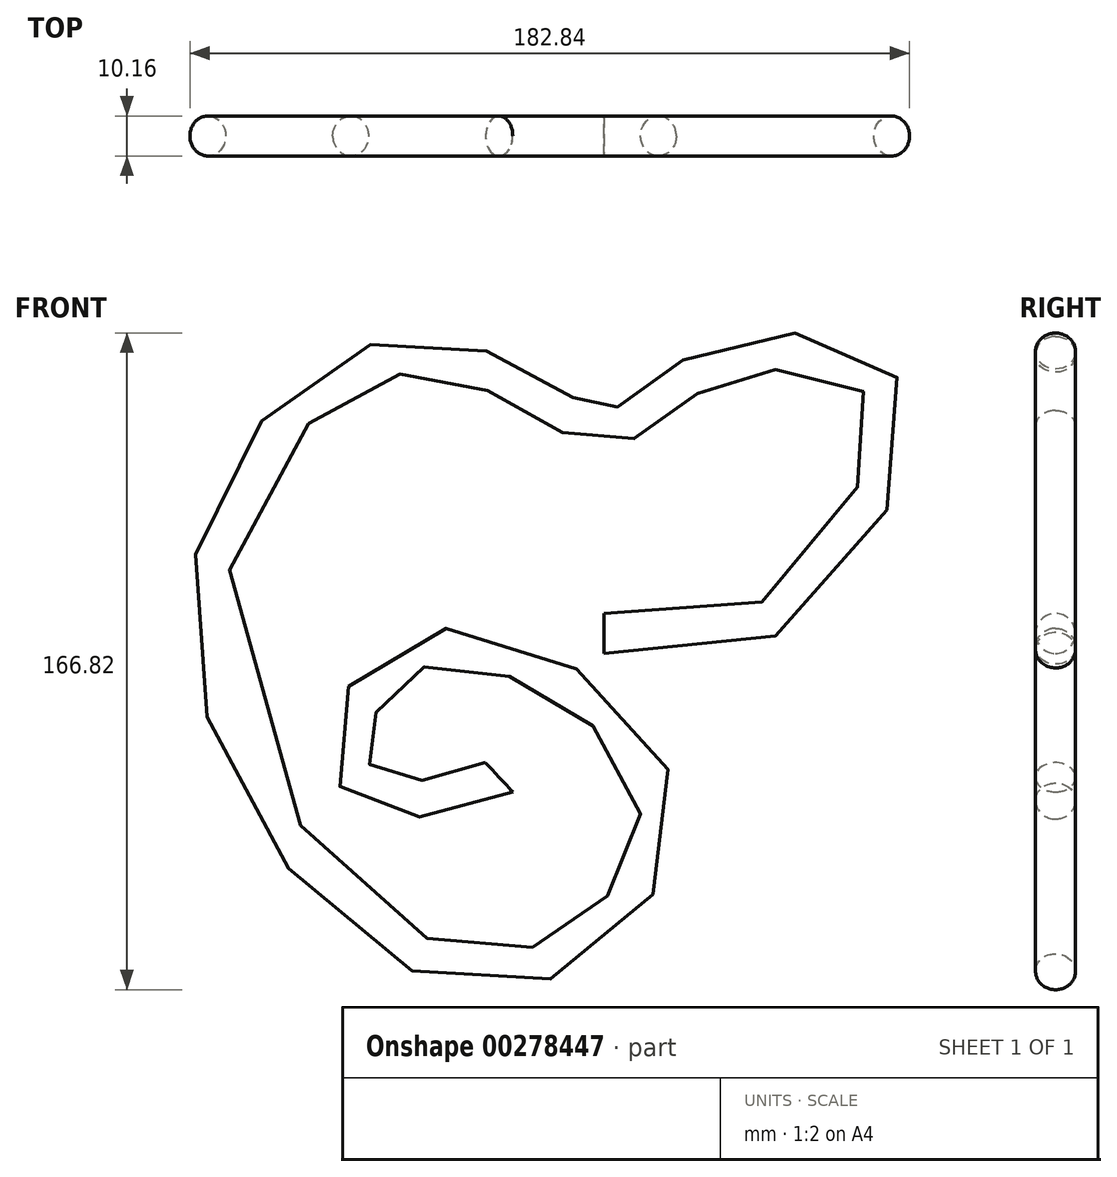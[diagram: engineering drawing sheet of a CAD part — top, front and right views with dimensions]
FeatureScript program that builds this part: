
annotation { "Feature Type Name" : "Feature", "Feature Type Description" : "" }
export const myFeature = defineFeature(function(context is Context, id is Id, definition is map)
    precondition{}
    {
        {
            var Q0;
            Q0=qCreatedBy(makeId("Front.planeOp"),FACE);
            var sketch = newSketch(context, id + "F0", { "sketchPlane" : qUnion([Q0])});
            skFitSpline(sketch, "E0", {"points": [v(0, 0) * mm, v(72.42, 58.1) * mm, v(26.07, 67.32) * mm, v(0, 52.5) * mm, v(-46.15, 70.86) * mm, v(-100.56, 7.63) * mm, v(-30.16, -85.83) * mm, v(12.97, -39.46) * mm, v(-50.5, -5.51) * mm, v(-61.54, -38.94) * mm, v(-26.63, -36.52) * mm], "startDerivative": vector(958.98, -469.75) * mm, "endDerivative": vector(538.14, 163.55) * mm});
            skSolve(sketch);
        }
        {
            var Q0;
            Q0=qCreatedBy(makeId("Right.planeOp"),FACE);
            var sketch = newSketch(context, id + "F1", { "sketchPlane" : qUnion([Q0])});
            skCircle(sketch, "E1", {"center": v(0, 0) * mm, "radius": 5.08 * mm});
            skSolve(sketch);
        }
        {
            var Q0;
            Q0=makeQuery(id+"F1.imprint","IMPRINT",FACE,{"disambiguationData":[TD([[makeQuery(id+"F1.imprint","IMPRINT",EDGE,{"derivedFrom":sQuery(id+"F1.wireOp",EDGE,"E1")}),1.0]])]});
            var Q1;
            Q1=sQuery(id+"F0.wireOp",EDGE,"E0");
            sweep(context, id + "F2", {"profiles" : qUnion([Q0]), "path" : qUnion([Q1])});
        }
    });
